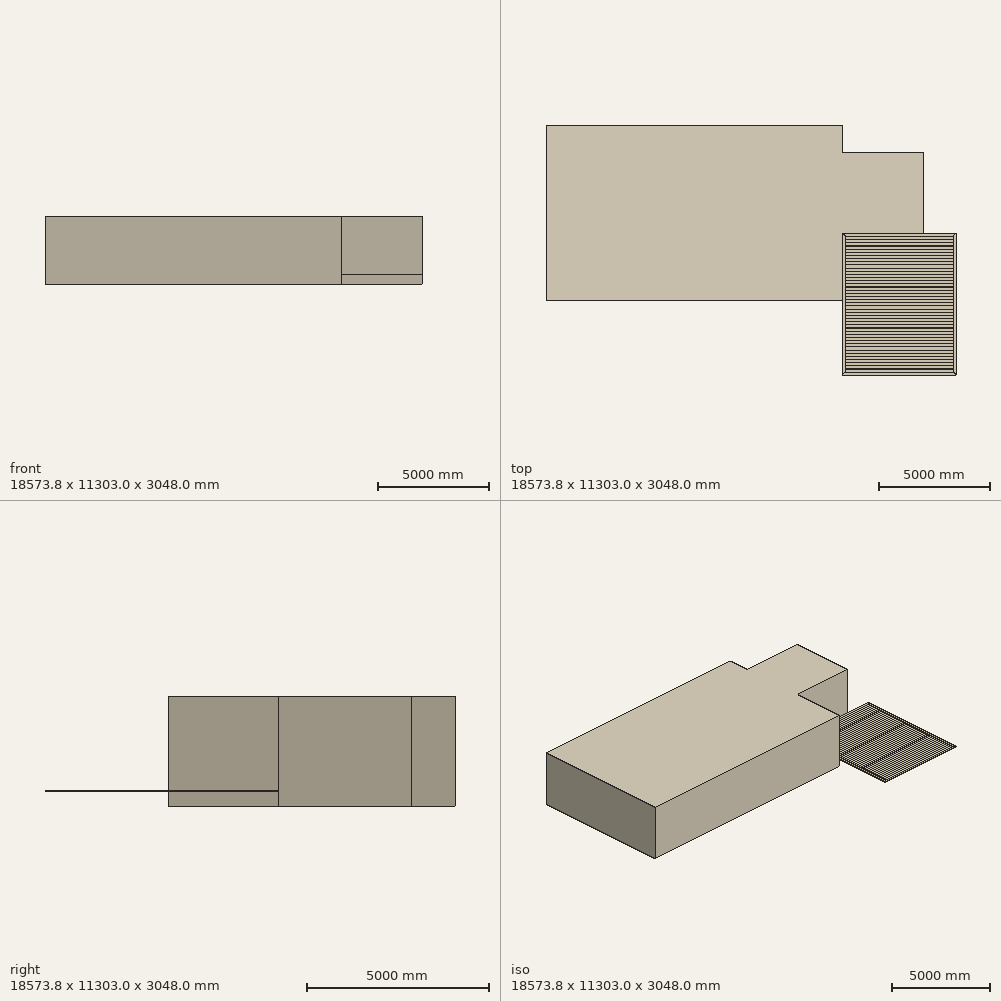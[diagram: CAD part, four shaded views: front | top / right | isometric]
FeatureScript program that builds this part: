
annotation { "Feature Type Name" : "Feature", "Feature Type Description" : "" }
export const myFeature = defineFeature(function(context is Context, id is Id, definition is map)
    precondition{}
    {
        {
            var Q0;
            Q0=qCreatedBy(makeId("Top.planeOp"),FACE);
            var sketch = newSketch(context, id + "F0", { "sketchPlane" : qUnion([Q0])});
            skLineSegment(sketch, "E0", {"start": v(-13411.2, 4876.8) * mm, "end": v(0, 4876.8) * mm});
            skLineSegment(sketch, "E1", {"start": v(0, 4876.8) * mm, "end": v(0, 3657.6) * mm});
            skLineSegment(sketch, "E2", {"start": v(0, 3657.6) * mm, "end": v(3657.6, 3657.6) * mm});
            skLineSegment(sketch, "E3", {"start": v(3657.6, 3657.6) * mm, "end": v(3657.6, 0) * mm});
            skLineSegment(sketch, "E4", {"start": v(3657.6, 0) * mm, "end": v(0, 0) * mm});
            skLineSegment(sketch, "E5", {"start": v(0, 0) * mm, "end": v(0, -3048) * mm});
            skLineSegment(sketch, "E6", {"start": v(0, -3048) * mm, "end": v(-13411.2, -3048) * mm});
            skLineSegment(sketch, "E7", {"start": v(-13411.2, 4876.8) * mm, "end": v(-13411.2, -3048) * mm});
            skSolve(sketch);
        }
        {
            var Q0;
            Q0 = qSketchRegion(id + "F0", true);
            extrude(context, id + "F1", {"entities" : qUnion([Q0]), "depth" : 3048 * mm, "offsetDistance" : 25.4 * mm});
        }
        {
            var Q0;
            Q0=makeQuery(id+"F1.opExtrude","CAP_FACE",FACE,{"disambiguationData":[OSD([sQuery(id+"F0.wireOp",EDGE,"E0"),sQuery(id+"F0.wireOp",EDGE,"E1"),sQuery(id+"F0.wireOp",EDGE,"E2"),sQuery(id+"F0.wireOp",EDGE,"E3"),sQuery(id+"F0.wireOp",EDGE,"E4"),sQuery(id+"F0.wireOp",EDGE,"E5"),sQuery(id+"F0.wireOp",EDGE,"E6"),sQuery(id+"F0.wireOp",EDGE,"E7")])],"isStart":true});
            cPlane(context, id + "F2", {"entities" : qUnion([Q0]), "cplaneType" : CPlaneType.OFFSET, "offset" : 431.8 * mm, "oppositeDirection" : true, "width" : 152.4 * mm, "height" : 152.4 * mm});
        }
        {
            var Q0;
            Q0=qCreatedBy(id+"F2.planeOp",FACE);
            var sketch = newSketch(context, id + "F3", { "sketchPlane" : qUnion([Q0])});
            skLineSegment(sketch, "E8", {"start": v(0, 0) * mm, "end": v(5162.55, 0) * mm});
            skLineSegment(sketch, "E9", {"start": v(5162.55, 0) * mm, "end": v(5022.85, 139.7) * mm});
            skLineSegment(sketch, "E10", {"start": v(5022.85, 139.7) * mm, "end": v(139.7, 139.7) * mm});
            skLineSegment(sketch, "E11", {"start": v(139.7, 139.7) * mm, "end": v(0, 0) * mm});
            skSolve(sketch);
        }
        {
            var Q0;
            Q0 = qSketchRegion(id + "F3", true);
            extrude(context, id + "F4", {"entities" : qUnion([Q0]), "operationType" : NewBodyOperationType.ADD, "oppositeDirection" : true, "depth" : 25.4 * mm, "offsetDistance" : 25.4 * mm});
        }
        {
            var Q0;
            Q0=qCreatedBy(id+"F2.planeOp",FACE);
            var sketch = newSketch(context, id + "F5", { "sketchPlane" : qUnion([Q0])});
            skLineSegment(sketch, "E12", {"start": v(0, 0.04) * mm, "end": v(0, 6426.24) * mm});
            skLineSegment(sketch, "E13", {"start": v(0, 6426.24) * mm, "end": v(139.7, 6286.54) * mm});
            skLineSegment(sketch, "E14", {"start": v(139.7, 6286.54) * mm, "end": v(139.7, 139.74) * mm});
            skLineSegment(sketch, "E15", {"start": v(139.7, 139.74) * mm, "end": v(0, 0.04) * mm});
            skSolve(sketch);
        }
        {
            var Q0;
            Q0 = qSketchRegion(id + "F5", true);
            extrude(context, id + "F6", {"entities" : qUnion([Q0]), "operationType" : NewBodyOperationType.ADD, "oppositeDirection" : true, "depth" : 25.4 * mm, "offsetDistance" : 25.4 * mm});
        }
        {
            var Q0;
            Q0=qCreatedBy(id+"F2.planeOp",FACE);
            var sketch = newSketch(context, id + "F7", { "sketchPlane" : qUnion([Q0])});
            skLineSegment(sketch, "E16.bottom", {"start": v(142.88, 142.88) * mm, "end": v(5019.68, 142.88) * mm});
            skLineSegment(sketch, "E16.top", {"start": v(142.88, 282.58) * mm, "end": v(5019.68, 282.58) * mm});
            skLineSegment(sketch, "E16.left", {"start": v(142.87, 142.88) * mm, "end": v(142.87, 282.58) * mm});
            skLineSegment(sketch, "E16.right", {"start": v(5019.68, 142.88) * mm, "end": v(5019.68, 282.58) * mm});
            skLineSegment(sketch, "E17.bottom", {"start": v(142.87, 285.75) * mm, "end": v(5019.68, 285.75) * mm});
            skLineSegment(sketch, "E17.top", {"start": v(142.87, 425.45) * mm, "end": v(5019.68, 425.45) * mm});
            skLineSegment(sketch, "E17.left", {"start": v(142.87, 285.75) * mm, "end": v(142.87, 425.45) * mm});
            skLineSegment(sketch, "E17.right", {"start": v(5019.68, 285.75) * mm, "end": v(5019.68, 425.45) * mm});
            skLineSegment(sketch, "E18.0.1.0", {"start": v(142.87, 568.32) * mm, "end": v(5019.68, 568.32) * mm});
            skLineSegment(sketch, "E18.0.1.1", {"start": v(142.87, 428.62) * mm, "end": v(142.87, 568.32) * mm});
            skLineSegment(sketch, "E18.0.1.2", {"start": v(142.87, 428.62) * mm, "end": v(5019.68, 428.62) * mm});
            skLineSegment(sketch, "E18.0.1.3", {"start": v(5019.68, 428.62) * mm, "end": v(5019.68, 568.32) * mm});
            skLineSegment(sketch, "E18.0.2.0", {"start": v(142.87, 711.2) * mm, "end": v(5019.68, 711.2) * mm});
            skLineSegment(sketch, "E18.0.2.1", {"start": v(142.87, 571.5) * mm, "end": v(142.87, 711.2) * mm});
            skLineSegment(sketch, "E18.0.2.2", {"start": v(142.87, 571.5) * mm, "end": v(5019.68, 571.5) * mm});
            skLineSegment(sketch, "E18.0.2.3", {"start": v(5019.68, 571.5) * mm, "end": v(5019.68, 711.2) * mm});
            skLineSegment(sketch, "E18.0.3.0", {"start": v(142.87, 854.07) * mm, "end": v(5019.68, 854.07) * mm});
            skLineSegment(sketch, "E18.0.3.1", {"start": v(142.87, 714.38) * mm, "end": v(142.87, 854.07) * mm});
            skLineSegment(sketch, "E18.0.3.2", {"start": v(142.87, 714.38) * mm, "end": v(5019.68, 714.38) * mm});
            skLineSegment(sketch, "E18.0.3.3", {"start": v(5019.68, 714.38) * mm, "end": v(5019.68, 854.07) * mm});
            skLineSegment(sketch, "E18.0.4.0", {"start": v(142.87, 996.95) * mm, "end": v(5019.68, 996.95) * mm});
            skLineSegment(sketch, "E18.0.4.1", {"start": v(142.87, 857.25) * mm, "end": v(142.87, 996.95) * mm});
            skLineSegment(sketch, "E18.0.4.2", {"start": v(142.87, 857.25) * mm, "end": v(5019.68, 857.25) * mm});
            skLineSegment(sketch, "E18.0.4.3", {"start": v(5019.68, 857.25) * mm, "end": v(5019.68, 996.95) * mm});
            skLineSegment(sketch, "E18.0.5.0", {"start": v(142.87, 1139.82) * mm, "end": v(5019.68, 1139.82) * mm});
            skLineSegment(sketch, "E18.0.5.1", {"start": v(142.87, 1000.12) * mm, "end": v(142.87, 1139.82) * mm});
            skLineSegment(sketch, "E18.0.5.2", {"start": v(142.87, 1000.12) * mm, "end": v(5019.68, 1000.12) * mm});
            skLineSegment(sketch, "E18.0.5.3", {"start": v(5019.68, 1000.12) * mm, "end": v(5019.68, 1139.83) * mm});
            skLineSegment(sketch, "E18.0.6.0", {"start": v(142.87, 1282.7) * mm, "end": v(5019.68, 1282.7) * mm});
            skLineSegment(sketch, "E18.0.6.1", {"start": v(142.87, 1143) * mm, "end": v(142.87, 1282.7) * mm});
            skLineSegment(sketch, "E18.0.6.2", {"start": v(142.87, 1143) * mm, "end": v(5019.68, 1143) * mm});
            skLineSegment(sketch, "E18.0.6.3", {"start": v(5019.68, 1143) * mm, "end": v(5019.68, 1282.7) * mm});
            skLineSegment(sketch, "E18.0.7.0", {"start": v(142.87, 1425.57) * mm, "end": v(5019.68, 1425.57) * mm});
            skLineSegment(sketch, "E18.0.7.1", {"start": v(142.87, 1285.87) * mm, "end": v(142.87, 1425.57) * mm});
            skLineSegment(sketch, "E18.0.7.2", {"start": v(142.87, 1285.87) * mm, "end": v(5019.68, 1285.87) * mm});
            skLineSegment(sketch, "E18.0.7.3", {"start": v(5019.68, 1285.87) * mm, "end": v(5019.68, 1425.57) * mm});
            skLineSegment(sketch, "E18.0.8.0", {"start": v(142.87, 1568.45) * mm, "end": v(5019.68, 1568.45) * mm});
            skLineSegment(sketch, "E18.0.8.1", {"start": v(142.87, 1428.75) * mm, "end": v(142.87, 1568.45) * mm});
            skLineSegment(sketch, "E18.0.8.2", {"start": v(142.87, 1428.75) * mm, "end": v(5019.68, 1428.75) * mm});
            skLineSegment(sketch, "E18.0.8.3", {"start": v(5019.68, 1428.75) * mm, "end": v(5019.68, 1568.45) * mm});
            skLineSegment(sketch, "E18.0.9.0", {"start": v(142.87, 1711.33) * mm, "end": v(5019.68, 1711.33) * mm});
            skLineSegment(sketch, "E18.0.9.1", {"start": v(142.87, 1571.62) * mm, "end": v(142.87, 1711.33) * mm});
            skLineSegment(sketch, "E18.0.9.2", {"start": v(142.87, 1571.62) * mm, "end": v(5019.68, 1571.62) * mm});
            skLineSegment(sketch, "E18.0.9.3", {"start": v(5019.68, 1571.62) * mm, "end": v(5019.68, 1711.33) * mm});
            skLineSegment(sketch, "E18.0.10.0", {"start": v(142.87, 1854.2) * mm, "end": v(5019.68, 1854.2) * mm});
            skLineSegment(sketch, "E18.0.10.1", {"start": v(142.87, 1714.5) * mm, "end": v(142.87, 1854.2) * mm});
            skLineSegment(sketch, "E18.0.10.2", {"start": v(142.87, 1714.5) * mm, "end": v(5019.68, 1714.5) * mm});
            skLineSegment(sketch, "E18.0.10.3", {"start": v(5019.68, 1714.5) * mm, "end": v(5019.68, 1854.2) * mm});
            skLineSegment(sketch, "E18.0.11.0", {"start": v(142.87, 1997.07) * mm, "end": v(5019.68, 1997.07) * mm});
            skLineSegment(sketch, "E18.0.11.1", {"start": v(142.87, 1857.37) * mm, "end": v(142.87, 1997.07) * mm});
            skLineSegment(sketch, "E18.0.11.2", {"start": v(142.87, 1857.37) * mm, "end": v(5019.68, 1857.37) * mm});
            skLineSegment(sketch, "E18.0.11.3", {"start": v(5019.68, 1857.37) * mm, "end": v(5019.68, 1997.07) * mm});
            skLineSegment(sketch, "E18.0.12.0", {"start": v(142.87, 2139.95) * mm, "end": v(5019.68, 2139.95) * mm});
            skLineSegment(sketch, "E18.0.12.1", {"start": v(142.87, 2000.25) * mm, "end": v(142.87, 2139.95) * mm});
            skLineSegment(sketch, "E18.0.12.2", {"start": v(142.87, 2000.25) * mm, "end": v(5019.68, 2000.25) * mm});
            skLineSegment(sketch, "E18.0.12.3", {"start": v(5019.68, 2000.25) * mm, "end": v(5019.68, 2139.95) * mm});
            skLineSegment(sketch, "E18.0.13.0", {"start": v(142.87, 2282.82) * mm, "end": v(5019.68, 2282.82) * mm});
            skLineSegment(sketch, "E18.0.13.1", {"start": v(142.87, 2143.12) * mm, "end": v(142.87, 2282.82) * mm});
            skLineSegment(sketch, "E18.0.13.2", {"start": v(142.87, 2143.12) * mm, "end": v(5019.68, 2143.12) * mm});
            skLineSegment(sketch, "E18.0.13.3", {"start": v(5019.68, 2143.12) * mm, "end": v(5019.68, 2282.82) * mm});
            skLineSegment(sketch, "E18.0.14.0", {"start": v(142.87, 2425.7) * mm, "end": v(5019.68, 2425.7) * mm});
            skLineSegment(sketch, "E18.0.14.1", {"start": v(142.87, 2286) * mm, "end": v(142.87, 2425.7) * mm});
            skLineSegment(sketch, "E18.0.14.2", {"start": v(142.87, 2286) * mm, "end": v(5019.68, 2286) * mm});
            skLineSegment(sketch, "E18.0.14.3", {"start": v(5019.68, 2286) * mm, "end": v(5019.68, 2425.7) * mm});
            skLineSegment(sketch, "E18.0.15.0", {"start": v(142.87, 2568.57) * mm, "end": v(5019.68, 2568.57) * mm});
            skLineSegment(sketch, "E18.0.15.1", {"start": v(142.87, 2428.87) * mm, "end": v(142.87, 2568.57) * mm});
            skLineSegment(sketch, "E18.0.15.2", {"start": v(142.87, 2428.87) * mm, "end": v(5019.68, 2428.87) * mm});
            skLineSegment(sketch, "E18.0.15.3", {"start": v(5019.68, 2428.87) * mm, "end": v(5019.68, 2568.57) * mm});
            skLineSegment(sketch, "E18.0.16.0", {"start": v(142.87, 2711.45) * mm, "end": v(5019.68, 2711.45) * mm});
            skLineSegment(sketch, "E18.0.16.1", {"start": v(142.87, 2571.75) * mm, "end": v(142.87, 2711.45) * mm});
            skLineSegment(sketch, "E18.0.16.2", {"start": v(142.87, 2571.75) * mm, "end": v(5019.68, 2571.75) * mm});
            skLineSegment(sketch, "E18.0.16.3", {"start": v(5019.68, 2571.75) * mm, "end": v(5019.68, 2711.45) * mm});
            skLineSegment(sketch, "E18.0.17.0", {"start": v(142.87, 2854.32) * mm, "end": v(5019.68, 2854.32) * mm});
            skLineSegment(sketch, "E18.0.17.1", {"start": v(142.87, 2714.62) * mm, "end": v(142.87, 2854.32) * mm});
            skLineSegment(sketch, "E18.0.17.2", {"start": v(142.87, 2714.62) * mm, "end": v(5019.68, 2714.62) * mm});
            skLineSegment(sketch, "E18.0.17.3", {"start": v(5019.68, 2714.62) * mm, "end": v(5019.68, 2854.32) * mm});
            skLineSegment(sketch, "E18.0.18.0", {"start": v(142.87, 2997.2) * mm, "end": v(5019.68, 2997.2) * mm});
            skLineSegment(sketch, "E18.0.18.1", {"start": v(142.87, 2857.5) * mm, "end": v(142.87, 2997.2) * mm});
            skLineSegment(sketch, "E18.0.18.2", {"start": v(142.87, 2857.5) * mm, "end": v(5019.68, 2857.5) * mm});
            skLineSegment(sketch, "E18.0.18.3", {"start": v(5019.68, 2857.5) * mm, "end": v(5019.68, 2997.2) * mm});
            skLineSegment(sketch, "E18.0.19.0", {"start": v(142.87, 3140.07) * mm, "end": v(5019.68, 3140.07) * mm});
            skLineSegment(sketch, "E18.0.19.1", {"start": v(142.87, 3000.37) * mm, "end": v(142.87, 3140.07) * mm});
            skLineSegment(sketch, "E18.0.19.2", {"start": v(142.87, 3000.37) * mm, "end": v(5019.68, 3000.37) * mm});
            skLineSegment(sketch, "E18.0.19.3", {"start": v(5019.68, 3000.37) * mm, "end": v(5019.68, 3140.07) * mm});
            skLineSegment(sketch, "E18.0.20.0", {"start": v(142.87, 3282.95) * mm, "end": v(5019.68, 3282.95) * mm});
            skLineSegment(sketch, "E18.0.20.1", {"start": v(142.87, 3143.25) * mm, "end": v(142.87, 3282.95) * mm});
            skLineSegment(sketch, "E18.0.20.2", {"start": v(142.87, 3143.25) * mm, "end": v(5019.68, 3143.25) * mm});
            skLineSegment(sketch, "E18.0.20.3", {"start": v(5019.68, 3143.25) * mm, "end": v(5019.68, 3282.95) * mm});
            skLineSegment(sketch, "E18.0.21.0", {"start": v(142.87, 3425.82) * mm, "end": v(5019.68, 3425.82) * mm});
            skLineSegment(sketch, "E18.0.21.1", {"start": v(142.87, 3286.12) * mm, "end": v(142.87, 3425.82) * mm});
            skLineSegment(sketch, "E18.0.21.2", {"start": v(142.87, 3286.12) * mm, "end": v(5019.68, 3286.12) * mm});
            skLineSegment(sketch, "E18.0.21.3", {"start": v(5019.68, 3286.12) * mm, "end": v(5019.68, 3425.82) * mm});
            skLineSegment(sketch, "E18.0.22.0", {"start": v(142.87, 3568.7) * mm, "end": v(5019.68, 3568.7) * mm});
            skLineSegment(sketch, "E18.0.22.1", {"start": v(142.87, 3429) * mm, "end": v(142.87, 3568.7) * mm});
            skLineSegment(sketch, "E18.0.22.2", {"start": v(142.87, 3429) * mm, "end": v(5019.68, 3429) * mm});
            skLineSegment(sketch, "E18.0.22.3", {"start": v(5019.68, 3429) * mm, "end": v(5019.68, 3568.7) * mm});
            skLineSegment(sketch, "E18.0.23.0", {"start": v(142.87, 3711.57) * mm, "end": v(5019.68, 3711.57) * mm});
            skLineSegment(sketch, "E18.0.23.1", {"start": v(142.87, 3571.87) * mm, "end": v(142.87, 3711.57) * mm});
            skLineSegment(sketch, "E18.0.23.2", {"start": v(142.87, 3571.87) * mm, "end": v(5019.68, 3571.87) * mm});
            skLineSegment(sketch, "E18.0.23.3", {"start": v(5019.68, 3571.87) * mm, "end": v(5019.68, 3711.57) * mm});
            skLineSegment(sketch, "E18.0.24.0", {"start": v(142.87, 3854.45) * mm, "end": v(5019.68, 3854.45) * mm});
            skLineSegment(sketch, "E18.0.24.1", {"start": v(142.87, 3714.75) * mm, "end": v(142.87, 3854.45) * mm});
            skLineSegment(sketch, "E18.0.24.2", {"start": v(142.87, 3714.75) * mm, "end": v(5019.68, 3714.75) * mm});
            skLineSegment(sketch, "E18.0.24.3", {"start": v(5019.68, 3714.75) * mm, "end": v(5019.68, 3854.45) * mm});
            skLineSegment(sketch, "E18.0.25.0", {"start": v(142.87, 3997.32) * mm, "end": v(5019.68, 3997.32) * mm});
            skLineSegment(sketch, "E18.0.25.1", {"start": v(142.87, 3857.62) * mm, "end": v(142.87, 3997.32) * mm});
            skLineSegment(sketch, "E18.0.25.2", {"start": v(142.87, 3857.62) * mm, "end": v(5019.68, 3857.62) * mm});
            skLineSegment(sketch, "E18.0.25.3", {"start": v(5019.68, 3857.62) * mm, "end": v(5019.68, 3997.32) * mm});
            skLineSegment(sketch, "E18.0.26.0", {"start": v(142.87, 4140.2) * mm, "end": v(5019.68, 4140.2) * mm});
            skLineSegment(sketch, "E18.0.26.1", {"start": v(142.87, 4000.5) * mm, "end": v(142.87, 4140.2) * mm});
            skLineSegment(sketch, "E18.0.26.2", {"start": v(142.87, 4000.5) * mm, "end": v(5019.68, 4000.5) * mm});
            skLineSegment(sketch, "E18.0.26.3", {"start": v(5019.68, 4000.5) * mm, "end": v(5019.68, 4140.2) * mm});
            skLineSegment(sketch, "E18.0.27.0", {"start": v(142.87, 4283.07) * mm, "end": v(5019.68, 4283.07) * mm});
            skLineSegment(sketch, "E18.0.27.1", {"start": v(142.87, 4143.37) * mm, "end": v(142.87, 4283.07) * mm});
            skLineSegment(sketch, "E18.0.27.2", {"start": v(142.87, 4143.37) * mm, "end": v(5019.68, 4143.37) * mm});
            skLineSegment(sketch, "E18.0.27.3", {"start": v(5019.68, 4143.37) * mm, "end": v(5019.68, 4283.07) * mm});
            skLineSegment(sketch, "E18.0.28.0", {"start": v(142.87, 4425.95) * mm, "end": v(5019.68, 4425.95) * mm});
            skLineSegment(sketch, "E18.0.28.1", {"start": v(142.87, 4286.25) * mm, "end": v(142.87, 4425.95) * mm});
            skLineSegment(sketch, "E18.0.28.2", {"start": v(142.87, 4286.25) * mm, "end": v(5019.68, 4286.25) * mm});
            skLineSegment(sketch, "E18.0.28.3", {"start": v(5019.68, 4286.25) * mm, "end": v(5019.68, 4425.95) * mm});
            skLineSegment(sketch, "E18.0.29.0", {"start": v(142.87, 4568.82) * mm, "end": v(5019.68, 4568.82) * mm});
            skLineSegment(sketch, "E18.0.29.1", {"start": v(142.87, 4429.12) * mm, "end": v(142.87, 4568.82) * mm});
            skLineSegment(sketch, "E18.0.29.2", {"start": v(142.87, 4429.12) * mm, "end": v(5019.68, 4429.12) * mm});
            skLineSegment(sketch, "E18.0.29.3", {"start": v(5019.68, 4429.12) * mm, "end": v(5019.68, 4568.82) * mm});
            skLineSegment(sketch, "E18.0.30.0", {"start": v(142.87, 4711.7) * mm, "end": v(5019.68, 4711.7) * mm});
            skLineSegment(sketch, "E18.0.30.1", {"start": v(142.87, 4572) * mm, "end": v(142.87, 4711.7) * mm});
            skLineSegment(sketch, "E18.0.30.2", {"start": v(142.87, 4572) * mm, "end": v(5019.68, 4572) * mm});
            skLineSegment(sketch, "E18.0.30.3", {"start": v(5019.68, 4572) * mm, "end": v(5019.68, 4711.7) * mm});
            skLineSegment(sketch, "E18.0.31.0", {"start": v(142.87, 4854.57) * mm, "end": v(5019.68, 4854.57) * mm});
            skLineSegment(sketch, "E18.0.31.1", {"start": v(142.87, 4714.87) * mm, "end": v(142.87, 4854.57) * mm});
            skLineSegment(sketch, "E18.0.31.2", {"start": v(142.87, 4714.87) * mm, "end": v(5019.68, 4714.87) * mm});
            skLineSegment(sketch, "E18.0.31.3", {"start": v(5019.68, 4714.87) * mm, "end": v(5019.68, 4854.57) * mm});
            skLineSegment(sketch, "E18.0.32.0", {"start": v(142.87, 4997.45) * mm, "end": v(5019.68, 4997.45) * mm});
            skLineSegment(sketch, "E18.0.32.1", {"start": v(142.87, 4857.75) * mm, "end": v(142.87, 4997.45) * mm});
            skLineSegment(sketch, "E18.0.32.2", {"start": v(142.87, 4857.75) * mm, "end": v(5019.68, 4857.75) * mm});
            skLineSegment(sketch, "E18.0.32.3", {"start": v(5019.68, 4857.75) * mm, "end": v(5019.68, 4997.45) * mm});
            skLineSegment(sketch, "E18.0.33.0", {"start": v(142.87, 5140.32) * mm, "end": v(5019.68, 5140.32) * mm});
            skLineSegment(sketch, "E18.0.33.1", {"start": v(142.87, 5000.62) * mm, "end": v(142.87, 5140.32) * mm});
            skLineSegment(sketch, "E18.0.33.2", {"start": v(142.87, 5000.62) * mm, "end": v(5019.68, 5000.62) * mm});
            skLineSegment(sketch, "E18.0.33.3", {"start": v(5019.68, 5000.62) * mm, "end": v(5019.68, 5140.32) * mm});
            skLineSegment(sketch, "E18.0.34.0", {"start": v(142.87, 5283.2) * mm, "end": v(5019.68, 5283.2) * mm});
            skLineSegment(sketch, "E18.0.34.1", {"start": v(142.87, 5143.5) * mm, "end": v(142.87, 5283.2) * mm});
            skLineSegment(sketch, "E18.0.34.2", {"start": v(142.87, 5143.5) * mm, "end": v(5019.68, 5143.5) * mm});
            skLineSegment(sketch, "E18.0.34.3", {"start": v(5019.68, 5143.5) * mm, "end": v(5019.68, 5283.2) * mm});
            skLineSegment(sketch, "E18.0.35.0", {"start": v(142.87, 5426.07) * mm, "end": v(5019.68, 5426.07) * mm});
            skLineSegment(sketch, "E18.0.35.1", {"start": v(142.87, 5286.38) * mm, "end": v(142.87, 5426.07) * mm});
            skLineSegment(sketch, "E18.0.35.2", {"start": v(142.87, 5286.38) * mm, "end": v(5019.68, 5286.38) * mm});
            skLineSegment(sketch, "E18.0.35.3", {"start": v(5019.68, 5286.38) * mm, "end": v(5019.68, 5426.07) * mm});
            skLineSegment(sketch, "E18.0.36.0", {"start": v(142.87, 5568.95) * mm, "end": v(5019.68, 5568.95) * mm});
            skLineSegment(sketch, "E18.0.36.1", {"start": v(142.87, 5429.25) * mm, "end": v(142.87, 5568.95) * mm});
            skLineSegment(sketch, "E18.0.36.2", {"start": v(142.87, 5429.25) * mm, "end": v(5019.68, 5429.25) * mm});
            skLineSegment(sketch, "E18.0.36.3", {"start": v(5019.68, 5429.25) * mm, "end": v(5019.68, 5568.95) * mm});
            skLineSegment(sketch, "E18.0.37.0", {"start": v(142.87, 5711.82) * mm, "end": v(5019.68, 5711.82) * mm});
            skLineSegment(sketch, "E18.0.37.1", {"start": v(142.87, 5572.12) * mm, "end": v(142.87, 5711.82) * mm});
            skLineSegment(sketch, "E18.0.37.2", {"start": v(142.87, 5572.12) * mm, "end": v(5019.68, 5572.12) * mm});
            skLineSegment(sketch, "E18.0.37.3", {"start": v(5019.68, 5572.12) * mm, "end": v(5019.68, 5711.82) * mm});
            skLineSegment(sketch, "E18.0.38.0", {"start": v(142.87, 5854.7) * mm, "end": v(5019.68, 5854.7) * mm});
            skLineSegment(sketch, "E18.0.38.1", {"start": v(142.87, 5715) * mm, "end": v(142.87, 5854.7) * mm});
            skLineSegment(sketch, "E18.0.38.2", {"start": v(142.87, 5715) * mm, "end": v(5019.68, 5715) * mm});
            skLineSegment(sketch, "E18.0.38.3", {"start": v(5019.68, 5715) * mm, "end": v(5019.68, 5854.7) * mm});
            skLineSegment(sketch, "E18.0.39.0", {"start": v(142.87, 5997.57) * mm, "end": v(5019.68, 5997.57) * mm});
            skLineSegment(sketch, "E18.0.39.1", {"start": v(142.87, 5857.87) * mm, "end": v(142.87, 5997.57) * mm});
            skLineSegment(sketch, "E18.0.39.2", {"start": v(142.87, 5857.87) * mm, "end": v(5019.68, 5857.87) * mm});
            skLineSegment(sketch, "E18.0.39.3", {"start": v(5019.68, 5857.87) * mm, "end": v(5019.68, 5997.57) * mm});
            skLineSegment(sketch, "E18.0.40.0", {"start": v(142.87, 6140.45) * mm, "end": v(5019.68, 6140.45) * mm});
            skLineSegment(sketch, "E18.0.40.1", {"start": v(142.87, 6000.75) * mm, "end": v(142.87, 6140.45) * mm});
            skLineSegment(sketch, "E18.0.40.2", {"start": v(142.87, 6000.75) * mm, "end": v(5019.68, 6000.75) * mm});
            skLineSegment(sketch, "E18.0.40.3", {"start": v(5019.68, 6000.75) * mm, "end": v(5019.68, 6140.45) * mm});
            skLineSegment(sketch, "E18.0.41.0", {"start": v(142.87, 6283.32) * mm, "end": v(5019.68, 6283.32) * mm});
            skLineSegment(sketch, "E18.0.41.1", {"start": v(142.87, 6143.62) * mm, "end": v(142.87, 6283.32) * mm});
            skLineSegment(sketch, "E18.0.41.2", {"start": v(142.87, 6143.62) * mm, "end": v(5019.68, 6143.62) * mm});
            skLineSegment(sketch, "E18.0.41.3", {"start": v(5019.68, 6143.62) * mm, "end": v(5019.68, 6283.32) * mm});
            skLineSegment(sketch, "E18.direction1", {"start": v(142.87, 425.45) * mm, "end": v(168.27, 425.45) * mm, "construction": true});
            skLineSegment(sketch, "E18.direction2", {"start": v(142.87, 425.45) * mm, "end": v(142.87, 568.32) * mm, "construction": true});
            skSolve(sketch);
        }
        {
            var Q0;
            Q0 = qSketchRegion(id + "F7", true);
            extrude(context, id + "F8", {"entities" : qUnion([Q0]), "oppositeDirection" : true, "depth" : 25.4 * mm, "offsetDistance" : 25.4 * mm});
        }
        {
            var Q0;
            Q0=qCreatedBy(id+"F2.planeOp",FACE);
            var sketch = newSketch(context, id + "F9", { "sketchPlane" : qUnion([Q0])});
            skLineSegment(sketch, "E19", {"start": v(5162.55, 0.04) * mm, "end": v(5022.85, 139.74) * mm});
            skLineSegment(sketch, "E20", {"start": v(5022.85, 139.74) * mm, "end": v(5022.85, 6286.5) * mm});
            skLineSegment(sketch, "E21", {"start": v(5022.85, 6286.5) * mm, "end": v(5162.55, 6426.2) * mm});
            skLineSegment(sketch, "E22", {"start": v(5162.55, 6426.2) * mm, "end": v(5162.55, 0.04) * mm});
            skSolve(sketch);
        }
        {
            var Q0;
            Q0 = qSketchRegion(id + "F9", true);
            extrude(context, id + "F10", {"entities" : qUnion([Q0]), "oppositeDirection" : true, "depth" : 25.4 * mm, "offsetDistance" : 25.4 * mm});
        }
        {
            var Q0;
            Q0=qCreatedBy(id+"F2.planeOp",FACE);
            var sketch = newSketch(context, id + "F11", { "sketchPlane" : qUnion([Q0])});
            skLineSegment(sketch, "E23", {"start": v(0.07, 6426.2) * mm, "end": v(5162.51, 6426.2) * mm});
            skLineSegment(sketch, "E24", {"start": v(5162.51, 6426.2) * mm, "end": v(5022.81, 6286.5) * mm});
            skLineSegment(sketch, "E25", {"start": v(5022.81, 6286.5) * mm, "end": v(139.77, 6286.5) * mm});
            skLineSegment(sketch, "E26", {"start": v(139.77, 6286.5) * mm, "end": v(0.07, 6426.2) * mm});
            skSolve(sketch);
        }
        {
            var Q0;
            Q0 = qSketchRegion(id + "F11", true);
            extrude(context, id + "F12", {"entities" : qUnion([Q0]), "oppositeDirection" : true, "depth" : 25.4 * mm, "offsetDistance" : 25.4 * mm});
        }
    });
